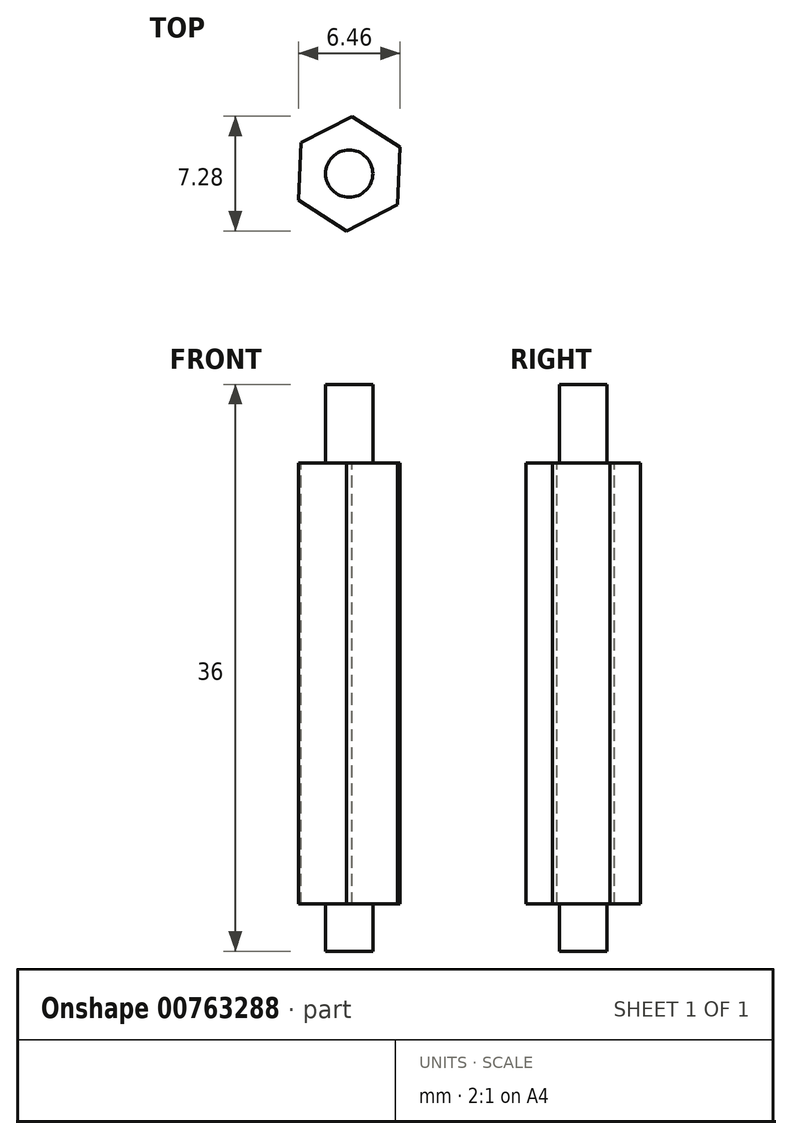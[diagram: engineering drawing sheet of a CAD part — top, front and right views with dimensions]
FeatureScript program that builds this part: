
annotation { "Feature Type Name" : "Feature", "Feature Type Description" : "" }
export const myFeature = defineFeature(function(context is Context, id is Id, definition is map)
    precondition{}
    {
        {
            var Q0;
            Q0=qCreatedBy(makeId("Top.planeOp"),FACE);
            var sketch = newSketch(context, id + "F0", { "sketchPlane" : qUnion([Q0])});
            skCircle(sketch, "E0.cCircle", {"center": v(0, 0) * mm, "radius": 3.15 * mm, "construction": true});
            skLineSegment(sketch, "E0.0", {"start": v(-0.16, -3.64) * mm, "end": v(-3.23, -1.68) * mm});
            skLineSegment(sketch, "E0.1", {"start": v(-3.23, -1.68) * mm, "end": v(-3.07, 1.96) * mm});
            skLineSegment(sketch, "E0.2", {"start": v(-3.07, 1.96) * mm, "end": v(0.16, 3.64) * mm});
            skLineSegment(sketch, "E0.3", {"start": v(0.16, 3.64) * mm, "end": v(3.23, 1.68) * mm});
            skLineSegment(sketch, "E0.4", {"start": v(3.23, 1.68) * mm, "end": v(3.07, -1.96) * mm});
            skLineSegment(sketch, "E0.5", {"start": v(3.07, -1.96) * mm, "end": v(-0.16, -3.64) * mm});
            skPoint(sketch, "E0.0.midPoint", {"position": v(-1.7, -2.66) * mm});
            skCircle(sketch, "E1", {"center": v(0, 0) * mm, "radius": 1.5 * mm});
            skSolve(sketch);
        }
        {
            var Q0;
            Q0 = qSketchRegion(id + "F0", true);
            var Q1;
            Q1=makeQuery(id+"F0.imprint","IMPRINT",FACE,{"disambiguationData":[TD([[makeQuery(id+"F0.imprint","IMPRINT",EDGE,{"derivedFrom":sQuery(id+"F0.wireOp",EDGE,"E1")}),1.0]])]});
            extrude(context, id + "F1", {"entities" : qUnion([Q0, Q1]), "oppositeDirection" : true, "depth" : 28 * mm, "offsetDistance" : 25 * mm});
        }
        {
            var Q0;
            Q0=makeQuery(id+"F0.imprint","IMPRINT",FACE,{"disambiguationData":[TD([[makeQuery(id+"F0.imprint","IMPRINT",EDGE,{"derivedFrom":sQuery(id+"F0.wireOp",EDGE,"E1")}),1.0]])]});
            extrude(context, id + "F2", {"entities" : qUnion([Q0]), "operationType" : NewBodyOperationType.ADD, "depth" : 5 * mm, "offsetDistance" : 25 * mm});
        }
        {
            var Q0;
            Q0=makeQuery(id+"F1.opExtrude","CAP_FACE",FACE,{"disambiguationData":[OSD([sQuery(id+"F0.wireOp",EDGE,"E0.0"),sQuery(id+"F0.wireOp",EDGE,"E0.1"),sQuery(id+"F0.wireOp",EDGE,"E0.2"),sQuery(id+"F0.wireOp",EDGE,"E0.3"),sQuery(id+"F0.wireOp",EDGE,"E0.4"),sQuery(id+"F0.wireOp",EDGE,"E0.5")])],"isStart":false});
            var sketch = newSketch(context, id + "F3", { "sketchPlane" : qUnion([Q0])});
            skCircle(sketch, "E2", {"center": v(0, 0) * mm, "radius": 1.5 * mm});
            skSolve(sketch);
        }
        {
            var Q0;
            Q0=makeQuery(id+"F3.imprint","IMPRINT",FACE,{"disambiguationData":[TD([[makeQuery(id+"F3.imprint","IMPRINT",EDGE,{"derivedFrom":sQuery(id+"F3.wireOp",EDGE,"E2")}),1.0]])]});
            extrude(context, id + "F4", {"entities" : qUnion([Q0]), "operationType" : NewBodyOperationType.ADD, "depth" : 3 * mm, "offsetDistance" : 25 * mm});
        }
    });
